# Revit family: ВУЕ П3_Б_Eng
name_source: partatom
category: Mechanical Equipment
units: mm (PartAtom-declared; Revit-internal decimal feet)

## family parameters
Always vertical = Yes
Classification = None
Cut with Voids When Loaded = No
Part Type = Normal
Room Calculation Point = No
Round Connector Dimension = Use Diameter
Shared = No
Work Plane-Based = No

## types (21) — shared parameters
00_20_Manufacturer = Vents
00_20_Name = Three-speed air handling unit
Casing Material = Steel, galvanized
Description = Heat- and sound-insulated casing
Frequency = 50 Hz
L3 = 138 mm  [stored 0.452756 ft]
L5 = 138 mm  [stored 0.452756 ft]
Load Classification = HVAC
Maintenance zone material = <By Category>
Manufacturer = Vents
Number of Fase = 1
URL = https://ventilation-system.com
Voltage = 230 V
a = 45 mm  [stored 0.147638 ft]
w = 50 mm  [stored 0.164042 ft]
zero-valued in all types: Default Elevation

## per-type parameters (varying)
- VUE 100 P3 L А3: 00_20_Type=VUE 100 P3 L А3; A=734 mm  [stored 2.40814 ft]; A1=600 mm; Amperage=0 A; Apparent Load=76 VA; B=481 mm  [stored 1.57808 ft]; B1=571 mm  [stored 1.87336 ft]; D=100 mm  [stored 0.328084 ft]; Dy=95 mm; Filter=G4/G4 + F8 (PM2.5 93 %); H1=223 mm  [stored 0.731627 ft]; Height=223 mm  [stored 0.731627 ft]; L=300 mm  [stored 0.984252 ft]; L1=92 mm  [stored 0.301837 ft]; L11=91 mm; L2=128 mm  [stored 0.419948 ft]; L22=91 mm; L33=113 mm  [stored 0.370735 ft]; L4=113 mm  [stored 0.370735 ft]; Length=734 mm  [stored 2.40814 ft]; Maximum Air Flow=160.0 m³/h; Power=76 W; Sound pressure level at 3 m distance=47 dBA; Temperature of moving air=-15...+40 °С; Weight=17.00 kg; Width=571 mm  [stored 1.87336 ft]
- VUE 200 P3 L А3: 00_20_Type=VUE 200 P3 L А3; A=987 mm; A1=854 mm  [stored 2.80184 ft]; Amperage=1 A; Apparent Load=145 VA; B=704 mm  [stored 2.30971 ft]; B1=793 mm  [stored 2.60171 ft]; D=150 mm; Dy=145 mm  [stored 0.475722 ft]; Filter=G4/G4 + F8 (PM2.5 93 %); H1=241 mm  [stored 0.790682 ft]; Height=241 mm  [stored 0.790682 ft]; L=480 mm  [stored 1.5748 ft]; L1=92 mm  [stored 0.301837 ft]; L11=112 mm  [stored 0.367454 ft]; L2=128 mm  [stored 0.419948 ft]; L22=112 mm  [stored 0.367454 ft]; L33=113 mm  [stored 0.370735 ft]; L4=113 mm  [stored 0.370735 ft]; Length=987 mm; Maximum Air Flow=280.0 m³/h; Power=141 W; Sound pressure level at 3 m distance=49 dBA; Temperature of moving air=-15...+40 °С; Weight=24.00 kg; Width=793 mm  [stored 2.60171 ft]
- VUE 300 P3 L А3: 00_20_Type=VUE 300 P3 L А3; A=987 mm; A1=854 mm  [stored 2.80184 ft]; Amperage=1 A; Apparent Load=193 VA; B=704 mm  [stored 2.30971 ft]; B1=793 mm  [stored 2.60171 ft]; D=150 mm; Dy=145 mm  [stored 0.475722 ft]; Filter=G4/G4 + F8 (PM2.5 93 %); H1=246 mm  [stored 0.807087 ft]; Height=246 mm  [stored 0.807087 ft]; L=480 mm  [stored 1.5748 ft]; L1=92 mm  [stored 0.301837 ft]; L11=112 mm  [stored 0.367454 ft]; L2=128 mm  [stored 0.419948 ft]; L22=112 mm  [stored 0.367454 ft]; L33=113 mm  [stored 0.370735 ft]; L4=113 mm  [stored 0.370735 ft]; Length=987 mm; Maximum Air Flow=340.0 m³/h; Power=193 W; Sound pressure level at 3 m distance=52 dBA; Temperature of moving air=-15...+40 °С; Weight=27.00 kg; Width=793 mm  [stored 2.60171 ft]
- VUE 450 P3 L А3: 00_20_Type=VUE 450 P3 L А3; A=1157 mm; A1=1024 mm; Amperage=2 A; Apparent Load=354 VA; B=754 mm  [stored 2.47375 ft]; B1=843 mm  [stored 2.76575 ft]; D=150 mm; Dy=145 mm  [stored 0.475722 ft]; Filter=G4/G4 + F8 (PM2.5 93 %); H1=296 mm  [stored 0.971129 ft]; Height=296 mm  [stored 0.971129 ft]; L=488 mm  [stored 1.60105 ft]; L1=92 mm  [stored 0.301837 ft]; L11=133 mm  [stored 0.436352 ft]; L2=128 mm  [stored 0.419948 ft]; L22=133 mm  [stored 0.436352 ft]; L33=113 mm  [stored 0.370735 ft]; L4=113 mm  [stored 0.370735 ft]; Length=1157 mm; Maximum Air Flow=500.0 m³/h; Power=354 W; Sound pressure level at 3 m distance=57 dBA; Temperature of moving air=-15...+40 °С; Weight=39.00 kg; Width=843 mm  [stored 2.76575 ft]
- VUE 150 P3 L А1: 00_20_Type=VUE 150 P3 L А1; A=947 mm; A1=854 mm  [stored 2.80184 ft]; Amperage=1 A; Apparent Load=138 VA; B=704 mm  [stored 2.30971 ft]; B1=793 mm  [stored 2.60171 ft]; D=99 mm  [stored 0.324803 ft]; Dy=94 mm  [stored 0.308399 ft]; Filter=G4/G4 and F8 (PM2.5 93 %); H1=247 mm; Height=247 mm; L=480 mm  [stored 1.5748 ft]; L1=92 mm  [stored 0.301837 ft]; L11=92 mm  [stored 0.301837 ft]; L2=128 mm  [stored 0.419948 ft]; L22=128 mm  [stored 0.419948 ft]; L33=113 mm  [stored 0.370735 ft]; L4=113 mm  [stored 0.370735 ft]; Length=947 mm; Maximum Air Flow=230.0 m³/h; Power=125 W; Sound pressure level at 3 m distance=49 dBA; Temperature of moving air=-25...+40 °С; Weight=26.00 kg; Width=793 mm  [stored 2.60171 ft]
- VUE 250 P3 L А1: 00_20_Type=VUE 250 P3 L А1; A=947 mm; A1=854 mm  [stored 2.80184 ft]; Amperage=1 A; Apparent Load=253 VA; B=704 mm  [stored 2.30971 ft]; B1=793 mm  [stored 2.60171 ft]; D=149 mm  [stored 0.488845 ft]; Dy=144 mm  [stored 0.472441 ft]; Filter=G4/G4 and F8 (PM2.5 83 %); H1=247 mm; Height=247 mm; L=480 mm  [stored 1.5748 ft]; L1=92 mm  [stored 0.301837 ft]; L11=92 mm  [stored 0.301837 ft]; L2=128 mm  [stored 0.419948 ft]; L22=128 mm  [stored 0.419948 ft]; L33=113 mm  [stored 0.370735 ft]; L4=113 mm  [stored 0.370735 ft]; Length=947 mm; Maximum Air Flow=370.0 m³/h; Power=250 W; Sound pressure level at 3 m distance=52 dBA; Temperature of moving air=-25...+40 °С; Weight=29.00 kg; Width=793 mm  [stored 2.60171 ft]
- VUE 350 P3 L А1: 00_20_Type=VUE 350 P3 L А1; A=1117 mm; A1=1024 mm; Amperage=1 A; Apparent Load=322 VA; B=754 mm  [stored 2.47375 ft]; B1=843 mm  [stored 2.76575 ft]; D=149 mm  [stored 0.488845 ft]; Dy=144 mm  [stored 0.472441 ft]; Filter=G4/G4 and F8 (PM2.5 87 %); H1=297 mm  [stored 0.974409 ft]; Height=297 mm  [stored 0.974409 ft]; L=488 mm  [stored 1.60105 ft]; L1=109 mm  [stored 0.357612 ft]; L11=109 mm  [stored 0.357612 ft]; L2=153 mm  [stored 0.501969 ft]; L22=153 mm  [stored 0.501969 ft]; L33=88 mm  [stored 0.288714 ft]; L4=88 mm  [stored 0.288714 ft]; Length=1117 mm; Maximum Air Flow=400.0 m³/h; Power=310 W; Sound pressure level at 3 m distance=57 dBA; Temperature of moving air=-25...+40 °С; Weight=42.00 kg; Width=843 mm  [stored 2.76575 ft]
- VUE 100 P3 R А3: 00_20_Type=VUE 100 P3 R А3; A=734 mm  [stored 2.40814 ft]; A1=600 mm; Amperage=0 A; Apparent Load=76 VA; B=481 mm  [stored 1.57808 ft]; B1=571 mm  [stored 1.87336 ft]; D=100 mm  [stored 0.328084 ft]; Dy=95 mm; Filter=G4/G4 + F8 (PM2.5 93 %); H1=223 mm  [stored 0.731627 ft]; Height=223 mm  [stored 0.731627 ft]; L=300 mm  [stored 0.984252 ft]; L1=92 mm  [stored 0.301837 ft]; L11=91 mm; L2=128 mm  [stored 0.419948 ft]; L22=91 mm; L33=113 mm  [stored 0.370735 ft]; L4=113 mm  [stored 0.370735 ft]; Length=734 mm  [stored 2.40814 ft]; Maximum Air Flow=160.0 m³/h; Power=76 W; Sound pressure level at 3 m distance=47 dBA; Temperature of moving air=-15...+40 °С; Weight=17.00 kg; Width=571 mm  [stored 1.87336 ft]
- VUE 150 P3 R А1: 00_20_Type=VUE 150 P3 L А1; A=947 mm; A1=854 mm  [stored 2.80184 ft]; Amperage=1 A; Apparent Load=138 VA; B=704 mm  [stored 2.30971 ft]; B1=793 mm  [stored 2.60171 ft]; D=99 mm  [stored 0.324803 ft]; Dy=94 mm  [stored 0.308399 ft]; Filter=G4/G4 and F8 (PM2.5 93 %); H1=247 mm; Height=247 mm; L=480 mm  [stored 1.5748 ft]; L1=92 mm  [stored 0.301837 ft]; L11=92 mm  [stored 0.301837 ft]; L2=128 mm  [stored 0.419948 ft]; L22=128 mm  [stored 0.419948 ft]; L33=113 mm  [stored 0.370735 ft]; L4=113 mm  [stored 0.370735 ft]; Length=947 mm; Maximum Air Flow=230.0 m³/h; Power=125 W; Sound pressure level at 3 m distance=49 dBA; Temperature of moving air=-25...+40 °С; Weight=26.00 kg; Width=793 mm  [stored 2.60171 ft]
- VUE 200 P3 R А3: 00_20_Type=VUE 200 P3 L А3; A=987 mm; A1=854 mm  [stored 2.80184 ft]; Amperage=1 A; Apparent Load=145 VA; B=704 mm  [stored 2.30971 ft]; B1=793 mm  [stored 2.60171 ft]; D=150 mm; Dy=145 mm  [stored 0.475722 ft]; Filter=G4/G4 + F8 (PM2.5 93 %); H1=241 mm  [stored 0.790682 ft]; Height=241 mm  [stored 0.790682 ft]; L=480 mm  [stored 1.5748 ft]; L1=92 mm  [stored 0.301837 ft]; L11=112 mm  [stored 0.367454 ft]; L2=128 mm  [stored 0.419948 ft]; L22=112 mm  [stored 0.367454 ft]; L33=113 mm  [stored 0.370735 ft]; L4=113 mm  [stored 0.370735 ft]; Length=987 mm; Maximum Air Flow=280.0 m³/h; Power=141 W; Sound pressure level at 3 m distance=49 dBA; Temperature of moving air=-15...+40 °С; Weight=24.00 kg; Width=793 mm  [stored 2.60171 ft]
- VUE 250 P3 R А1: 00_20_Type=VUE 250 P3 R А1; A=947 mm; A1=854 mm  [stored 2.80184 ft]; Amperage=1 A; Apparent Load=253 VA; B=704 mm  [stored 2.30971 ft]; B1=793 mm  [stored 2.60171 ft]; D=149 mm  [stored 0.488845 ft]; Dy=144 mm  [stored 0.472441 ft]; Filter=G4/G4 and F8 (PM2.5 83 %); H1=247 mm; Height=247 mm; L=480 mm  [stored 1.5748 ft]; L1=92 mm  [stored 0.301837 ft]; L11=92 mm  [stored 0.301837 ft]; L2=128 mm  [stored 0.419948 ft]; L22=128 mm  [stored 0.419948 ft]; L33=113 mm  [stored 0.370735 ft]; L4=113 mm  [stored 0.370735 ft]; Length=947 mm; Maximum Air Flow=370.0 m³/h; Power=250 W; Sound pressure level at 3 m distance=52 dBA; Temperature of moving air=-25...+40 °С; Weight=29.00 kg; Width=793 mm  [stored 2.60171 ft]
- VUE 300 P3 R А3: 00_20_Type=VUE 300 P3 R А3; A=987 mm; A1=854 mm  [stored 2.80184 ft]; Amperage=1 A; Apparent Load=193 VA; B=704 mm  [stored 2.30971 ft]; B1=793 mm  [stored 2.60171 ft]; D=150 mm; Dy=145 mm  [stored 0.475722 ft]; Filter=G4/G4 + F8 (PM2.5 93 %); H1=246 mm  [stored 0.807087 ft]; Height=246 mm  [stored 0.807087 ft]; L=480 mm  [stored 1.5748 ft]; L1=92 mm  [stored 0.301837 ft]; L11=112 mm  [stored 0.367454 ft]; L2=128 mm  [stored 0.419948 ft]; L22=112 mm  [stored 0.367454 ft]; L33=113 mm  [stored 0.370735 ft]; L4=113 mm  [stored 0.370735 ft]; Length=987 mm; Maximum Air Flow=340.0 m³/h; Power=193 W; Sound pressure level at 3 m distance=52 dBA; Temperature of moving air=-15...+40 °С; Weight=27.00 kg; Width=793 mm  [stored 2.60171 ft]
- VUE 350 P3 R А1: 00_20_Type=VUE 350 P3 R А1; A=1117 mm; A1=1024 mm; Amperage=1 A; Apparent Load=322 VA; B=754 mm  [stored 2.47375 ft]; B1=843 mm  [stored 2.76575 ft]; D=149 mm  [stored 0.488845 ft]; Dy=144 mm  [stored 0.472441 ft]; Filter=G4/G4 and F8 (PM2.5 87 %); H1=297 mm  [stored 0.974409 ft]; Height=297 mm  [stored 0.974409 ft]; L=488 mm  [stored 1.60105 ft]; L1=109 mm  [stored 0.357612 ft]; L11=109 mm  [stored 0.357612 ft]; L2=153 mm  [stored 0.501969 ft]; L22=153 mm  [stored 0.501969 ft]; L33=88 mm  [stored 0.288714 ft]; L4=88 mm  [stored 0.288714 ft]; Length=1117 mm; Maximum Air Flow=400.0 m³/h; Power=310 W; Sound pressure level at 3 m distance=57 dBA; Temperature of moving air=-25...+40 °С; Weight=42.00 kg; Width=843 mm  [stored 2.76575 ft]
- VUE 450 P3 R А3: 00_20_Type=VUE 450 P3 R А3; A=1157 mm; A1=1024 mm; Amperage=2 A; Apparent Load=354 VA; B=754 mm  [stored 2.47375 ft]; B1=843 mm  [stored 2.76575 ft]; D=150 mm; Dy=145 mm  [stored 0.475722 ft]; Filter=G4/G4 + F8 (PM2.5 93 %); H1=296 mm  [stored 0.971129 ft]; Height=296 mm  [stored 0.971129 ft]; L=488 mm  [stored 1.60105 ft]; L1=92 mm  [stored 0.301837 ft]; L11=133 mm  [stored 0.436352 ft]; L2=128 mm  [stored 0.419948 ft]; L22=133 mm  [stored 0.436352 ft]; L33=113 mm  [stored 0.370735 ft]; L4=113 mm  [stored 0.370735 ft]; Length=1157 mm; Maximum Air Flow=500.0 m³/h; Power=354 W; Sound pressure level at 3 m distance=57 dBA; Temperature of moving air=-15...+40 °С; Weight=39.00 kg; Width=843 mm  [stored 2.76575 ft]
- VUE 100 P3B ЕС L А14: 00_20_Type=VUE 100 P3B ЕС L А14; A=734 mm  [stored 2.40814 ft]; A1=600 mm; Amperage=1 A; Apparent Load=115 VA; B=481 mm  [stored 1.57808 ft]; B1=571 mm  [stored 1.87336 ft]; D=100 mm  [stored 0.328084 ft]; Dy=95 mm; Filter=G4/G4 + F8 (PM2.5 93 %); H1=229 mm; Height=229 mm; L=300 mm  [stored 0.984252 ft]; L1=92 mm  [stored 0.301837 ft]; L11=91 mm; L2=128 mm  [stored 0.419948 ft]; L22=91 mm; L33=113 mm  [stored 0.370735 ft]; L4=113 mm  [stored 0.370735 ft]; Length=734 mm  [stored 2.40814 ft]; Maximum Air Flow=170.0 m³/h; Power=66 W; Sound pressure level at 3 m distance=30 dBA; Temperature of moving air=-15...+40 °С; Weight=17.00 kg; Width=571 mm  [stored 1.87336 ft]
- VUE 150 P3B ЕС L А14: 00_20_Type=VUE 150 P3B ЕС L А14; A=987 mm; A1=854 mm  [stored 2.80184 ft]; Amperage=1 A; Apparent Load=161 VA; B=704 mm  [stored 2.30971 ft]; B1=793 mm  [stored 2.60171 ft]; D=100 mm  [stored 0.328084 ft]; Dy=95 mm; Filter=G4/G4 and F8 (PM2.5 93 %); H1=241 mm  [stored 0.790682 ft]; Height=241 mm  [stored 0.790682 ft]; L=480 mm  [stored 1.5748 ft]; L1=92 mm  [stored 0.301837 ft]; L11=112 mm  [stored 0.367454 ft]; L2=128 mm  [stored 0.419948 ft]; L22=112 mm  [stored 0.367454 ft]; L33=113 mm  [stored 0.370735 ft]; L4=113 mm  [stored 0.370735 ft]; Length=987 mm; Maximum Air Flow=215.0 m³/h; Power=83 W; Sound pressure level at 3 m distance=32 dBA; Temperature of moving air=-25...+40 °С; Weight=26.00 kg; Width=793 mm  [stored 2.60171 ft]
- VUE 150 P3B ЕС R А14: 00_20_Type=VUE 150 P3B ЕС R А14; A=987 mm; A1=854 mm  [stored 2.80184 ft]; Amperage=1 A; Apparent Load=161 VA; B=704 mm  [stored 2.30971 ft]; B1=793 mm  [stored 2.60171 ft]; D=100 mm  [stored 0.328084 ft]; Dy=95 mm; Filter=G4/G4 and F8 (PM2.5 93 %); H1=241 mm  [stored 0.790682 ft]; Height=241 mm  [stored 0.790682 ft]; L=480 mm  [stored 1.5748 ft]; L1=92 mm  [stored 0.301837 ft]; L11=112 mm  [stored 0.367454 ft]; L2=128 mm  [stored 0.419948 ft]; L22=112 mm  [stored 0.367454 ft]; L33=113 mm  [stored 0.370735 ft]; L4=113 mm  [stored 0.370735 ft]; Length=987 mm; Maximum Air Flow=215.0 m³/h; Power=83 W; Sound pressure level at 3 m distance=32 dBA; Temperature of moving air=-25...+40 °С; Weight=26.00 kg; Width=793 mm  [stored 2.60171 ft]
- VUE 250 P3B ЕС L А14: 00_20_Type=VUE 250 P3B ЕС L А14; A=987 mm; A1=854 mm  [stored 2.80184 ft]; Amperage=1 A; Apparent Load=161 VA; B=704 mm  [stored 2.30971 ft]; B1=793 mm  [stored 2.60171 ft]; D=150 mm; Dy=145 mm  [stored 0.475722 ft]; Filter=G4/G4 and F8 (PM2.5 93 %); H1=246 mm  [stored 0.807087 ft]; Height=246 mm  [stored 0.807087 ft]; L=480 mm  [stored 1.5748 ft]; L1=92 mm  [stored 0.301837 ft]; L11=112 mm  [stored 0.367454 ft]; L2=128 mm  [stored 0.419948 ft]; L22=112 mm  [stored 0.367454 ft]; L33=113 mm  [stored 0.370735 ft]; L4=113 mm  [stored 0.370735 ft]; Length=987 mm; Maximum Air Flow=300.0 m³/h; Power=84 W; Sound pressure level at 3 m distance=36 dBA; Temperature of moving air=-25...+40 °С; Weight=29.00 kg; Width=793 mm  [stored 2.60171 ft]
- VUE 250 P3B ЕС R А14: 00_20_Type=VUE 250 P3B ЕС R А14; A=987 mm; A1=854 mm  [stored 2.80184 ft]; Amperage=1 A; Apparent Load=161 VA; B=704 mm  [stored 2.30971 ft]; B1=793 mm  [stored 2.60171 ft]; D=150 mm; Dy=145 mm  [stored 0.475722 ft]; Filter=G4/G4 and F8 (PM2.5 93 %); H1=246 mm  [stored 0.807087 ft]; Height=246 mm  [stored 0.807087 ft]; L=480 mm  [stored 1.5748 ft]; L1=92 mm  [stored 0.301837 ft]; L11=112 mm  [stored 0.367454 ft]; L2=128 mm  [stored 0.419948 ft]; L22=112 mm  [stored 0.367454 ft]; L33=113 mm  [stored 0.370735 ft]; L4=113 mm  [stored 0.370735 ft]; Length=987 mm; Maximum Air Flow=300.0 m³/h; Power=84 W; Sound pressure level at 3 m distance=36 dBA; Temperature of moving air=-25...+40 °С; Weight=29.00 kg; Width=793 mm  [stored 2.60171 ft]
- VUE 350 P3B ЕС L А14: 00_20_Type=VUE 350 P3B ЕС L А14; A=1157 mm; A1=1024 mm; Amperage=1 A; Apparent Load=299 VA; B=754 mm  [stored 2.47375 ft]; B1=843 mm  [stored 2.76575 ft]; D=150 mm; Dy=145 mm  [stored 0.475722 ft]; Filter=G4/G4 and F8 (PM2.5 93 %); H1=296 mm  [stored 0.971129 ft]; Height=296 mm  [stored 0.971129 ft]; L=488 mm  [stored 1.60105 ft]; L1=109 mm  [stored 0.357612 ft]; L11=133 mm  [stored 0.436352 ft]; L2=153 mm  [stored 0.501969 ft]; L22=133 mm  [stored 0.436352 ft]; L33=88 mm  [stored 0.288714 ft]; L4=88 mm  [stored 0.288714 ft]; Length=1157 mm; Maximum Air Flow=430.0 m³/h; Power=171 W; Sound pressure level at 3 m distance=46 dBA; Temperature of moving air=-25...+40 °С; Weight=42.00 kg; Width=843 mm  [stored 2.76575 ft]
- VUE 350 P3B ЕС R А14: 00_20_Type=VUE 350 P3B ЕС R А14; A=1157 mm; A1=1024 mm; Amperage=1 A; Apparent Load=299 VA; B=754 mm  [stored 2.47375 ft]; B1=843 mm  [stored 2.76575 ft]; D=150 mm; Dy=145 mm  [stored 0.475722 ft]; Filter=G4/G4 and F8 (PM2.5 93 %); H1=296 mm  [stored 0.971129 ft]; Height=296 mm  [stored 0.971129 ft]; L=488 mm  [stored 1.60105 ft]; L1=109 mm  [stored 0.357612 ft]; L11=133 mm  [stored 0.436352 ft]; L2=153 mm  [stored 0.501969 ft]; L22=133 mm  [stored 0.436352 ft]; L33=88 mm  [stored 0.288714 ft]; L4=88 mm  [stored 0.288714 ft]; Length=1157 mm; Maximum Air Flow=430.0 m³/h; Power=171 W; Sound pressure level at 3 m distance=46 dBA; Temperature of moving air=-25...+40 °С; Weight=42.00 kg; Width=843 mm  [stored 2.76575 ft]

note: [stored X ft] marks values corroborated as IEEE doubles in the binary element streams (Revit-internal decimal feet)
